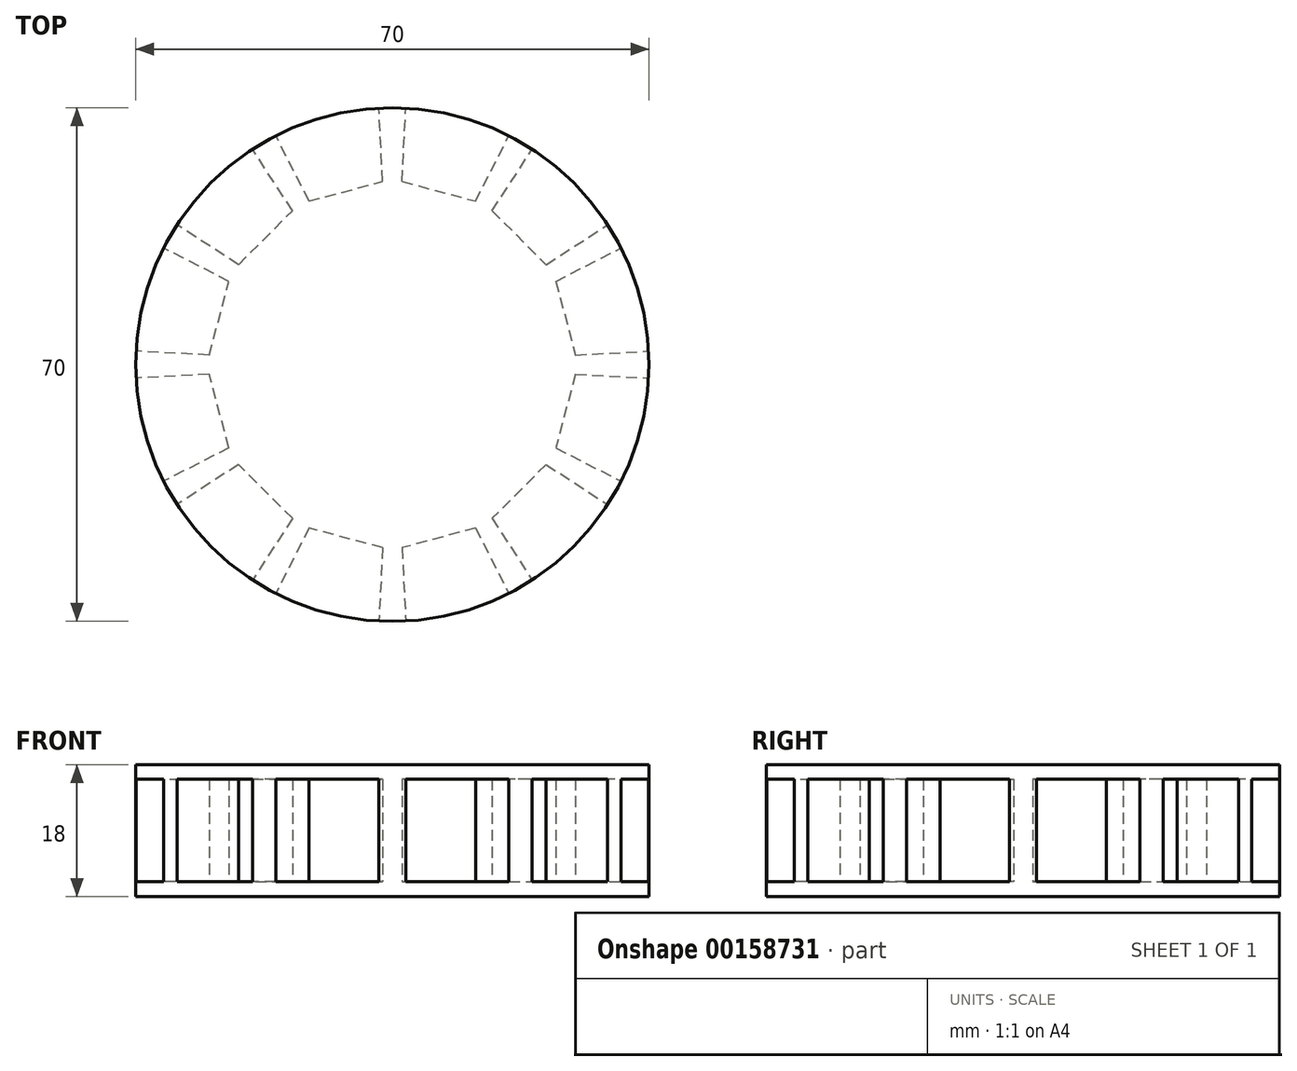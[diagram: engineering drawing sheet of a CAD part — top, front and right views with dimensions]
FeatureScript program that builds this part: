
annotation { "Feature Type Name" : "Feature", "Feature Type Description" : "" }
export const myFeature = defineFeature(function(context is Context, id is Id, definition is map)
    precondition{}
    {
        {
            var Q0;
            Q0=qCreatedBy(makeId("Top.planeOp"),FACE);
            var sketch = newSketch(context, id + "F0", { "sketchPlane" : qUnion([Q0])});
            skCircle(sketch, "E0", {"center": v(0, 0) * mm, "radius": 35 * mm});
            skSolve(sketch);
        }
        {
            var Q0;
            Q0 = qSketchRegion(id + "F0", true);
            extrude(context, id + "F1", {"entities" : qUnion([Q0]), "depth" : 18 * mm});
        }
        {
            var Q0;
            Q0=makeQuery(id+"F1.opExtrude","CAP_FACE",FACE,{"disambiguationData":[OSD([sQuery(id+"F0.wireOp",EDGE,"E0")])],"isStart":true});
            var sketch = newSketch(context, id + "F2", { "sketchPlane" : qUnion([Q0])});
            skLineSegment(sketch, "E1", {"start": v(34.95, 1.83) * mm, "end": v(24.97, 1.3) * mm});
            skLineSegment(sketch, "E2", {"start": v(31.19, 15.89) * mm, "end": v(22.28, 11.35) * mm});
            skLineSegment(sketch, "E3", {"start": v(31.19, 15.89) * mm, "end": v(29.35, 19.06) * mm});
            skLineSegment(sketch, "E4", {"start": v(29.35, 19.06) * mm, "end": v(20.97, 13.62) * mm});
            skLineSegment(sketch, "E5", {"start": v(19.06, 29.35) * mm, "end": v(13.62, 20.97) * mm});
            skLineSegment(sketch, "E6", {"start": v(19.06, 29.35) * mm, "end": v(15.89, 31.19) * mm});
            skLineSegment(sketch, "E7", {"start": v(15.89, 31.19) * mm, "end": v(11.35, 22.28) * mm});
            skLineSegment(sketch, "E8", {"start": v(1.83, 34.95) * mm, "end": v(1.3, 24.97) * mm});
            skArc(sketch, "E9", {"start": v(15.89, 31.19) * mm, "mid": v(9.06, 33.8) * mm, "end": v(1.83, 34.95) * mm});
            skLineSegment(sketch, "E10", {"start": v(1.3, 24.97) * mm, "end": v(11.35, 22.28) * mm});
            skLineSegment(sketch, "E11", {"start": v(13.62, 20.97) * mm, "end": v(20.97, 13.62) * mm});
            skLineSegment(sketch, "E12", {"start": v(22.28, 11.35) * mm, "end": v(24.97, 1.3) * mm});
            skArc(sketch, "E13.trimOffspring", {"start": v(29.35, 19.06) * mm, "mid": v(24.75, 24.75) * mm, "end": v(19.06, 29.35) * mm});
            skArc(sketch, "E14.trimOffspring", {"start": v(34.95, 1.83) * mm, "mid": v(33.8, 9.06) * mm, "end": v(31.19, 15.89) * mm});
            skLineSegment(sketch, "E15.1.0", {"start": v(-34.95, 1.83) * mm, "end": v(-24.97, 1.3) * mm});
            skArc(sketch, "E15.1.1", {"start": v(-31.19, 15.89) * mm, "mid": v(-33.8, 9.06) * mm, "end": v(-34.95, 1.83) * mm});
            skLineSegment(sketch, "E15.1.2", {"start": v(-31.19, 15.89) * mm, "end": v(-22.28, 11.35) * mm});
            skLineSegment(sketch, "E15.1.3", {"start": v(-24.97, 1.3) * mm, "end": v(-22.28, 11.35) * mm});
            skLineSegment(sketch, "E15.1.4", {"start": v(-29.35, 19.06) * mm, "end": v(-20.97, 13.62) * mm});
            skLineSegment(sketch, "E15.1.5", {"start": v(-20.97, 13.62) * mm, "end": v(-13.62, 20.97) * mm});
            skArc(sketch, "E15.1.6", {"start": v(-19.06, 29.35) * mm, "mid": v(-24.75, 24.75) * mm, "end": v(-29.35, 19.06) * mm});
            skLineSegment(sketch, "E15.1.7", {"start": v(-19.06, 29.35) * mm, "end": v(-13.62, 20.97) * mm});
            skLineSegment(sketch, "E15.1.8", {"start": v(-15.89, 31.19) * mm, "end": v(-11.35, 22.28) * mm});
            skLineSegment(sketch, "E15.1.9", {"start": v(-11.35, 22.28) * mm, "end": v(-1.3, 24.97) * mm});
            skArc(sketch, "E15.1.10", {"start": v(-1.83, 34.95) * mm, "mid": v(-9.06, 33.8) * mm, "end": v(-15.89, 31.19) * mm});
            skLineSegment(sketch, "E15.1.11", {"start": v(-1.83, 34.95) * mm, "end": v(-1.3, 24.97) * mm});
            skLineSegment(sketch, "E15.2.0", {"start": v(-1.83, -34.95) * mm, "end": v(-1.3, -24.97) * mm});
            skArc(sketch, "E15.2.1", {"start": v(-15.89, -31.19) * mm, "mid": v(-9.06, -33.8) * mm, "end": v(-1.83, -34.95) * mm});
            skLineSegment(sketch, "E15.2.2", {"start": v(-15.89, -31.19) * mm, "end": v(-11.35, -22.28) * mm});
            skLineSegment(sketch, "E15.2.3", {"start": v(-1.3, -24.97) * mm, "end": v(-11.35, -22.28) * mm});
            skLineSegment(sketch, "E15.2.4", {"start": v(-19.06, -29.35) * mm, "end": v(-13.62, -20.97) * mm});
            skLineSegment(sketch, "E15.2.5", {"start": v(-13.62, -20.97) * mm, "end": v(-20.97, -13.62) * mm});
            skArc(sketch, "E15.2.6", {"start": v(-29.35, -19.06) * mm, "mid": v(-24.75, -24.75) * mm, "end": v(-19.06, -29.35) * mm});
            skLineSegment(sketch, "E15.2.7", {"start": v(-29.35, -19.06) * mm, "end": v(-20.97, -13.62) * mm});
            skLineSegment(sketch, "E15.2.8", {"start": v(-31.19, -15.89) * mm, "end": v(-22.28, -11.35) * mm});
            skLineSegment(sketch, "E15.2.9", {"start": v(-22.28, -11.35) * mm, "end": v(-24.97, -1.3) * mm});
            skArc(sketch, "E15.2.10", {"start": v(-34.95, -1.83) * mm, "mid": v(-33.8, -9.06) * mm, "end": v(-31.19, -15.89) * mm});
            skLineSegment(sketch, "E15.2.11", {"start": v(-34.95, -1.83) * mm, "end": v(-24.97, -1.3) * mm});
            skLineSegment(sketch, "E15.3.0", {"start": v(34.95, -1.83) * mm, "end": v(24.97, -1.3) * mm});
            skArc(sketch, "E15.3.1", {"start": v(31.19, -15.89) * mm, "mid": v(33.8, -9.06) * mm, "end": v(34.95, -1.83) * mm});
            skLineSegment(sketch, "E15.3.2", {"start": v(31.19, -15.89) * mm, "end": v(22.28, -11.35) * mm});
            skLineSegment(sketch, "E15.3.3", {"start": v(24.97, -1.3) * mm, "end": v(22.28, -11.35) * mm});
            skLineSegment(sketch, "E15.3.4", {"start": v(29.35, -19.06) * mm, "end": v(20.97, -13.62) * mm});
            skLineSegment(sketch, "E15.3.5", {"start": v(20.97, -13.62) * mm, "end": v(13.62, -20.97) * mm});
            skArc(sketch, "E15.3.6", {"start": v(19.06, -29.35) * mm, "mid": v(24.75, -24.75) * mm, "end": v(29.35, -19.06) * mm});
            skLineSegment(sketch, "E15.3.7", {"start": v(19.06, -29.35) * mm, "end": v(13.62, -20.97) * mm});
            skLineSegment(sketch, "E15.3.8", {"start": v(15.89, -31.19) * mm, "end": v(11.35, -22.28) * mm});
            skLineSegment(sketch, "E15.3.9", {"start": v(11.35, -22.28) * mm, "end": v(1.3, -24.97) * mm});
            skArc(sketch, "E15.3.10", {"start": v(1.83, -34.95) * mm, "mid": v(9.06, -33.8) * mm, "end": v(15.89, -31.19) * mm});
            skLineSegment(sketch, "E15.3.11", {"start": v(1.83, -34.95) * mm, "end": v(1.3, -24.97) * mm});
            skPoint(sketch, "E16.startSnap0", {"position": v(-25.16, -16.34) * mm});
            skSolve(sketch);
        }
        {
            var Q0;
            Q0 = qSketchRegion(id + "F2", true);
            extrude(context, id + "F3", {"entities" : qUnion([Q0]), "operationType" : NewBodyOperationType.REMOVE, "oppositeDirection" : true, "depth" : 16 * mm});
        }
        {
            var Q0;
            Q0=makeQuery(id+"F1.opExtrude","CAP_FACE",FACE,{"disambiguationData":[OSD([sQuery(id+"F0.wireOp",EDGE,"E0")])],"isStart":true});
            var sketch = newSketch(context, id + "F4", { "sketchPlane" : qUnion([Q0])});
            skCircle(sketch, "E17", {"center": v(0, 0) * mm, "radius": 35 * mm});
            skSolve(sketch);
        }
        {
            var Q0;
            Q0 = qSketchRegion(id + "F4", true);
            extrude(context, id + "F5", {"entities" : qUnion([Q0]), "operationType" : NewBodyOperationType.ADD, "oppositeDirection" : true, "depth" : 2 * mm});
        }
    });
